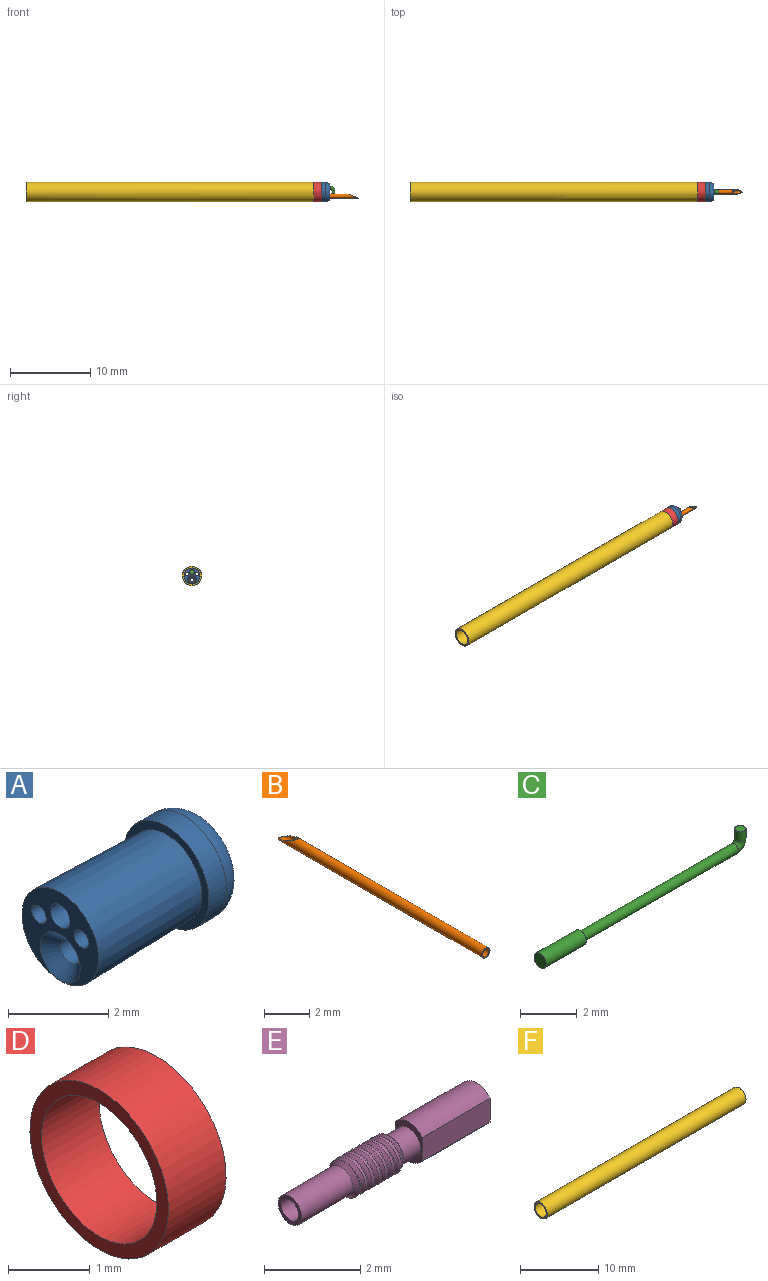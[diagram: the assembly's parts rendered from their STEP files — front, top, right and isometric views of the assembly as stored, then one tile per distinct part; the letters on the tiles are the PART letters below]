
ASSEMBLY  parts=6 mates=5
PART A: 11 faces, bbox 4x2.6x2.6 mm
  f0: plane 1.4x1.33mm, normal (1,0,0), area 0.9mm2, adj f4,f6,f7,f8,f9
  f1: plane 2.4x2.4mm, normal (-1,0,0), area 1.4mm2, adj f2,f5
  f2: cone r=1mm half-angle=1.5deg, axis (-1,0,0), area 19.6mm2, adj f1,f3
  f3: plane 2.16x2.16mm, normal (-1,0,0), area 2.2mm2, adj f2,f6,f7,f8,f10
  f4: torus R=0.7mm, axis (-1,0,0), area 4.9mm2, adj f0,f5,f6,f7,f8,f9
  f5: cylinder r=1.2mm len=2.4mm, axis (-1,0,0), area 3.8mm2, adj f1,f4
  f6: cylinder r=0.28mm len=4mm, axis (1,0,0), area 6.9mm2, adj f0,f3,f4
  f7: cylinder r=0.2mm len=4mm, axis (1,0,0), area 5.2mm2, adj f0,f3,f4
  f8: cylinder r=0.2mm len=4mm, axis (1,0,0), area 5.2mm2, adj f0,f3,f4
  f9: cylinder r=0.28mm len=3.71mm, axis (1,0,0), area 6.4mm2, adj f0,f4,f10
  f10: cone r=0.56mm half-angle=45deg, axis (-1,0,0), area 1.1mm2, adj f3,f9
PART B: 6 faces, bbox 0.5x13x0.5 mm
  f0: cylinder r=0.2mm len=12.88mm, axis (0,1,0), area 16mm2, adj f2,f3
  f1: cylinder r=0.26mm len=13mm, axis (0,1,0), area 19.8mm2, adj f2,f3,f4,f5
  f2: plane 1.21x0.52mm, normal (0,0.39,0.92), area 0.1mm2, adj f0,f1,f4,f5
  f3: plane 0.51x0.51mm, normal (0,-1,0), area 0.1mm2, adj f0,f1
  f4: plane 0.36x0.23mm, normal (-0.84,0.54,0), area 0mm2, adj f1,f2
  f5: plane 0.36x0.23mm, normal (0.84,0.54,0), area 0mm2, adj f1,f2
PART C: 7 faces, bbox 10.2x0.6x1 mm
  f0: cylinder r=0.2mm len=7.7mm, axis (1,0,0), area 9.7mm2, adj f2,f5
  f1: plane 0.4x0.4mm, normal (0,0,1), area 0.1mm2, adj f3
  f2: torus R=0.3mm, axis (0,-1,0), area 0.6mm2, adj f0,f3
  f3: cylinder r=0.2mm len=0.4mm, axis (0,0,1), area 0.5mm2, adj f1,f2
  f4: cylinder r=0.3mm len=2mm, axis (-1,0,0), area 3.8mm2, adj f5,f6
  f5: plane 0.61x0.61mm, normal (1,0,0), area 0.2mm2, adj f0,f4
  f6: plane 0.61x0.61mm, normal (-1,0,0), area 0.3mm2, adj f4
PART D: 4 faces, bbox 1x2.4x2.4 mm
  f0: cylinder r=1mm len=2mm, axis (-1,0,0), area 6.3mm2, adj f2,f3
  f1: cylinder r=1.2mm len=2.4mm, axis (-1,0,0), area 7.5mm2, adj f2,f3
  f2: plane 2.4x2.4mm, normal (1,0,0), area 1.4mm2, adj f0,f1
  f3: plane 2.4x2.4mm, normal (-1,0,0), area 1.4mm2, adj f0,f1
PART E: 15 faces, bbox 5.5x0.9x1.1 mm
  f0: cone r=0.45mm half-angle=45deg, axis (1,0,0), area 0.3mm2, adj f4,f5,f13,f14
  f1: cone r=0.35mm half-angle=45deg, axis (-1,0,0), area 0.3mm2, adj f2,f5,f13,f14
  f2: cylinder r=0.35mm len=0.7mm, axis (1,0,0), area 1.1mm2, adj f1,f9
  f3: cylinder r=0.26mm len=5.5mm, axis (1,0,0), area 8.8mm2, adj f6,f10
  f4: cylinder r=0.35mm len=1.5mm, axis (1,0,0), area 3.3mm2, adj f0,f10
  f5: cylinder r=0.45mm len=1.3mm, axis (1,0,0), area 1.3mm2, adj f0,f1,f13,f14
  f6: plane 1x0.8mm, normal (1,0,0), area 0.5mm2, adj f3,f7,f8,f11,f12
  f7: cylinder r=0.5mm len=2mm, axis (1,0,0), area 1.9mm2, adj f6,f9,f11,f12
  f8: cylinder r=0.5mm len=2mm, axis (1,0,0), area 1.9mm2, adj f6,f9,f11,f12
  f9: plane 1x0.8mm, normal (-1,0,0), area 0.3mm2, adj f2,f7,f8,f11,f12
  f10: plane 0.7x0.7mm, normal (-1,0,0), area 0.2mm2, adj f3,f4
  f11: plane 2x0.6mm, normal (0,1,0), area 1.2mm2, adj f6,f7,f8,f9
  f12: plane 2x0.6mm, normal (0,-1,0), area 1.2mm2, adj f6,f7,f8,f9
  f13: bspline ~1.51x1.05mm, area 1.5mm2, adj f0,f1,f5,f14
  f14: bspline ~1.51x1.05mm, area 1.5mm2, adj f0,f1,f5,f13
PART F: 4 faces, bbox 35.9x2.4x2.4 mm
  f0: cylinder r=1mm len=35.9mm, axis (-1,0,0), area 225.6mm2, adj f1,f3
  f1: plane 2.4x2.4mm, normal (1,0,0), area 1.4mm2, adj f0,f2
  f2: cylinder r=1.2mm len=35.9mm, axis (-1,0,0), area 270.7mm2, adj f1,f3
  f3: plane 2.4x2.4mm, normal (-1,0,0), area 1.4mm2, adj f0,f2
PLACE A rot(axis=(-1,0,0),0deg) t=(20.33,0.55,0.07)mm
PLACE B rot(axis=(0,0,-1),90deg) t=(25.73,0.55,-0.44)mm
PLACE C rot(axis=(1,0,0),180deg) t=(12.63,0.55,0.57)mm
PLACE D rot(axis=(-1,0,0),0deg) t=(-60.01,0.55,0.07)mm
PLACE E rot(axis=(1,0,0),90deg) t=(-19.15,0.55,-0.44)mm
PLACE F t=(-60.01,0.55,0.07)mm
MATE fastened D.f0 <-> F.f0  axis (-1,0,0) through (20.23,0.55,0.07)mm
MATE slider A.f6 <-> C.f0  axis (1,0,0) through (22.23,0.55,0.57)mm
MATE slider B.f0 <-> A.f9  axis (1,0,0) through (19.27,0.55,-0.44)mm
MATE fastened D.f0 <-> A.f2  axis (1,0,0) through (21.23,0.55,0.07)mm
MATE fastened B.f0 <-> E.f0  axis (1,0,0) through (12.73,0.55,-0.44)mm
